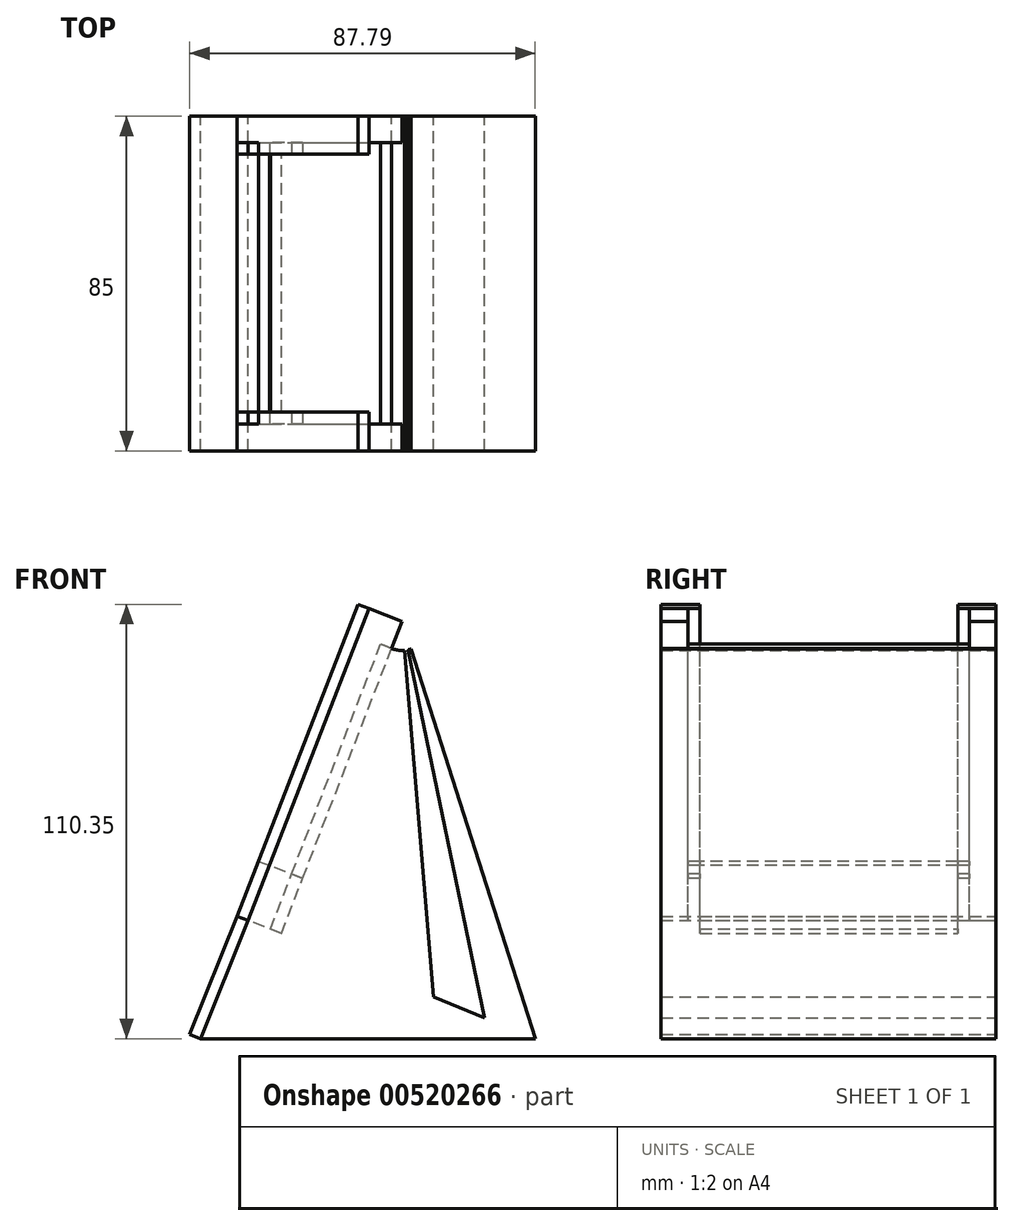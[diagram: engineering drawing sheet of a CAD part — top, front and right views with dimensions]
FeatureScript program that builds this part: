
annotation { "Feature Type Name" : "Feature", "Feature Type Description" : "" }
export const myFeature = defineFeature(function(context is Context, id is Id, definition is map)
    precondition{}
    {
        {
            var Q0;
            Q0=qCreatedBy(makeId("Front.planeOp"),FACE);
            var sketch = newSketch(context, id + "F0", { "sketchPlane" : qUnion([Q0])});
            skLineSegment(sketch, "E0", {"start": v(-20.42, 0) * mm, "end": v(-8.32, 30) * mm});
            skLineSegment(sketch, "E1", {"start": v(-8.32, 30) * mm, "end": v(64.58, 0) * mm});
            skLineSegment(sketch, "E2", {"start": v(64.58, 0) * mm, "end": v(-20.42, 0) * mm});
            skLineSegment(sketch, "E3", {"start": v(-8.32, 30) * mm, "end": v(22.36, 109.27) * mm});
            skLineSegment(sketch, "E4", {"start": v(22.36, 109.27) * mm, "end": v(30.76, 106.02) * mm});
            skLineSegment(sketch, "E5", {"start": v(30.76, 106.02) * mm, "end": v(64.58, 0) * mm});
            skLineSegment(sketch, "E6", {"start": v(-8.32, 30) * mm, "end": v(0, 26.58) * mm});
            skLineSegment(sketch, "E7", {"start": v(0, 26.58) * mm, "end": v(-8.32, 30) * mm});
            skLineSegment(sketch, "E8", {"start": v(0, 26.58) * mm, "end": v(30.76, 106.02) * mm});
            skLineSegment(sketch, "E9", {"start": v(12.92, 21.26) * mm, "end": v(30.76, 106.02) * mm});
            skLineSegment(sketch, "E10", {"start": v(25.83, 15.95) * mm, "end": v(30.76, 106.02) * mm});
            skLineSegment(sketch, "E11", {"start": v(30.76, 106.02) * mm, "end": v(38.75, 10.63) * mm});
            skLineSegment(sketch, "E12", {"start": v(51.67, 5.32) * mm, "end": v(30.76, 106.02) * mm});
            skArc(sketch, "E13", {"start": v(33, 98.99) * mm, "mid": v(30.53, 98.64) * mm, "end": v(28.1, 99.13) * mm});
            skSolve(sketch);
        }
        {
            var Q0;
            Q0=makeQuery(id+"F0.imprint","IMPRINT",FACE,{"disambiguationData":[TD([[makeQuery(id+"F0.imprint","IMPRINT",EDGE,{"derivedFrom":sQuery(id+"F0.wireOp",EDGE,"E3")}),-1.0]])]});
            var Q1;
            {var subQ1=sQuery(id+"F0.wireOp",EDGE,"E1");var subQ3=sQuery(id+"F0.wireOp",EDGE,"E9");var subQ4=makeQuery(id+"F0.imprint","INTERSECT",VERTEX,{"derivedFrom":[subQ1,subQ3]});Q1=makeQuery(id+"F0.imprint","IMPRINT",FACE,{"disambiguationData":[TD([[makeQuery(id+"F0.imprint","IMPRINT",EDGE,{"disambiguationData":[TD([[subQ4,-1.0]])],"derivedFrom":subQ3}),1.0]])]});}
            var Q2;
            {var subQ1=sQuery(id+"F0.wireOp",EDGE,"E9");var subQ3=sQuery(id+"F0.wireOp",EDGE,"E13");var subQ4=makeQuery(id+"F0.imprint","INTERSECT",VERTEX,{"derivedFrom":[subQ1,subQ3]});Q2=makeQuery(id+"F0.imprint","IMPRINT",FACE,{"disambiguationData":[TD([[makeQuery(id+"F0.imprint","IMPRINT",EDGE,{"disambiguationData":[TD([[subQ4,1.0]])],"derivedFrom":subQ3}),-1.0]])]});}
            var Q3;
            {var subQ1=sQuery(id+"F0.wireOp",EDGE,"E10");var subQ3=sQuery(id+"F0.wireOp",EDGE,"E13");var subQ4=makeQuery(id+"F0.imprint","INTERSECT",VERTEX,{"derivedFrom":[subQ1,subQ3]});Q3=makeQuery(id+"F0.imprint","IMPRINT",FACE,{"disambiguationData":[TD([[makeQuery(id+"F0.imprint","IMPRINT",EDGE,{"disambiguationData":[TD([[subQ4,1.0]])],"derivedFrom":subQ3}),-1.0]])]});}
            var Q4;
            {var subQ1=sQuery(id+"F0.wireOp",EDGE,"E8");var subQ3=sQuery(id+"F0.wireOp",EDGE,"E13");var subQ4=makeQuery(id+"F0.imprint","INTERSECT",VERTEX,{"derivedFrom":[subQ1,subQ3]});Q4=makeQuery(id+"F0.imprint","IMPRINT",FACE,{"disambiguationData":[TD([[makeQuery(id+"F0.imprint","IMPRINT",EDGE,{"disambiguationData":[TD([[subQ4,1.0]])],"derivedFrom":subQ3}),-1.0]])]});}
            var Q5;
            {var subQ1=sQuery(id+"F0.wireOp",EDGE,"E11");var subQ3=sQuery(id+"F0.wireOp",EDGE,"E13");var subQ4=makeQuery(id+"F0.imprint","INTERSECT",VERTEX,{"derivedFrom":[subQ1,subQ3]});Q5=makeQuery(id+"F0.imprint","IMPRINT",FACE,{"disambiguationData":[TD([[makeQuery(id+"F0.imprint","IMPRINT",EDGE,{"disambiguationData":[TD([[subQ4,1.0]])],"derivedFrom":subQ3}),-1.0]])]});}
            var Q6;
            {var subQ1=sQuery(id+"F0.wireOp",EDGE,"E5");var subQ3=sQuery(id+"F0.wireOp",EDGE,"E13");var subQ4=makeQuery(id+"F0.imprint","INTERSECT",VERTEX,{"derivedFrom":[subQ1,subQ3]});Q6=makeQuery(id+"F0.imprint","IMPRINT",FACE,{"disambiguationData":[TD([[makeQuery(id+"F0.imprint","IMPRINT",EDGE,{"disambiguationData":[TD([[subQ4,-1.0]])],"derivedFrom":subQ3}),-1.0]])]});}
            var Q7;
            {var subQ0=sQuery(id+"F0.wireOp",EDGE,"E10");var subQ1=sQuery(id+"F0.wireOp",EDGE,"E1");var subQ2=makeQuery(id+"F0.imprint","INTERSECT",VERTEX,{"derivedFrom":[subQ1,subQ0]});Q7=makeQuery(id+"F0.imprint","IMPRINT",FACE,{"disambiguationData":[TD([[makeQuery(id+"F0.imprint","IMPRINT",EDGE,{"disambiguationData":[TD([[subQ2,-1.0]])],"derivedFrom":subQ1}),1.0]])]});}
            var Q8;
            {var subQ1=sQuery(id+"F0.wireOp",EDGE,"E1");var subQ3=sQuery(id+"F0.wireOp",EDGE,"E12");var subQ4=makeQuery(id+"F0.imprint","INTERSECT",VERTEX,{"derivedFrom":[subQ1,subQ3]});Q8=makeQuery(id+"F0.imprint","IMPRINT",FACE,{"disambiguationData":[TD([[makeQuery(id+"F0.imprint","IMPRINT",EDGE,{"disambiguationData":[TD([[subQ4,-1.0]])],"derivedFrom":subQ3}),-1.0]])]});}
            var Q9;
            Q9=makeQuery(id+"F0.imprint","IMPRINT",FACE,{"disambiguationData":[TD([[makeQuery(id+"F0.imprint","IMPRINT",EDGE,{"derivedFrom":sQuery(id+"F0.wireOp",EDGE,"E0")}),-1.0]])]});
            extrude(context, id + "F1", {"entities" : qUnion([Q0, Q1, Q2, Q3, Q4, Q5, Q6, Q7, Q8, Q9]), "endBound" : BoundingType.SYMMETRIC, "depth" : 85 * mm, "offsetDistance" : 25 * mm});
        }
        {
            var Q0;
            Q0=makeQuery(id+"F1.opExtrude","SWEPT_FACE",FACE,{"disambiguationData":[OSD([sQuery(id+"F0.wireOp",EDGE,"E3")])]});
            var sketch = newSketch(context, id + "F2", { "sketchPlane" : qUnion([Q0])});
            skLineSegment(sketch, "E14.bottom", {"start": v(-35.85, 24.97) * mm, "end": v(35.65, 24.97) * mm});
            skLineSegment(sketch, "E14.top", {"start": v(-35.85, 121.84) * mm, "end": v(35.65, 121.84) * mm});
            skLineSegment(sketch, "E14.left", {"start": v(-35.85, 24.97) * mm, "end": v(-35.85, 121.84) * mm});
            skLineSegment(sketch, "E14.right", {"start": v(35.65, 24.97) * mm, "end": v(35.65, 121.84) * mm});
            skLineSegment(sketch, "E15.bottom", {"start": v(-0.1, 24.97) * mm, "end": v(35.65, 24.97) * mm});
            skLineSegment(sketch, "E15.right", {"start": v(35.65, 24.97) * mm, "end": v(35.65, 35.08) * mm});
            skLineSegment(sketch, "E16.bottom", {"start": v(-35.85, 24.97) * mm, "end": v(-0.1, 24.97) * mm});
            skLineSegment(sketch, "E16.left", {"start": v(-35.85, 24.97) * mm, "end": v(-35.85, 35.08) * mm});
            skLineSegment(sketch, "E17.top", {"start": v(-35.85, 39.97) * mm, "end": v(35.65, 39.97) * mm});
            skLineSegment(sketch, "E17.left", {"start": v(-35.85, 24.97) * mm, "end": v(-35.85, 39.97) * mm});
            skLineSegment(sketch, "E17.right", {"start": v(35.65, 24.97) * mm, "end": v(35.65, 39.97) * mm});
            skLineSegment(sketch, "E18.bottom", {"start": v(-35.85, 24.97) * mm, "end": v(-32.85, 24.97) * mm});
            skLineSegment(sketch, "E18.top", {"start": v(-35.85, 109.97) * mm, "end": v(-32.85, 109.97) * mm});
            skLineSegment(sketch, "E18.left", {"start": v(-35.85, 24.97) * mm, "end": v(-35.85, 109.97) * mm});
            skLineSegment(sketch, "E18.right", {"start": v(-32.85, 24.97) * mm, "end": v(-32.85, 109.97) * mm});
            skLineSegment(sketch, "E19.bottom", {"start": v(35.65, 24.97) * mm, "end": v(32.65, 24.97) * mm});
            skLineSegment(sketch, "E19.top", {"start": v(35.65, 109.97) * mm, "end": v(32.65, 109.97) * mm});
            skLineSegment(sketch, "E19.left", {"start": v(35.65, 24.97) * mm, "end": v(35.65, 109.97) * mm});
            skLineSegment(sketch, "E19.right", {"start": v(32.65, 24.97) * mm, "end": v(32.65, 109.97) * mm});
            skSolve(sketch);
        }
        {
            var Q0;
            {var subQ5=sQuery(id+"F2.wireOp",EDGE,"E19.top");Q0=makeQuery(id+"F2.imprint","IMPRINT",FACE,{"disambiguationData":[TD([[makeQuery(id+"F2.imprint","IMPRINT",EDGE,{"derivedFrom":subQ5}),1.0]])]});}
            var Q1;
            {var subQ0=sQuery(id+"F2.wireOp",EDGE,"E18.right");var subQ1=sQuery(id+"F2.wireOp",EDGE,"E17.top");var subQ2=makeQuery(id+"F2.imprint","INTERSECT",VERTEX,{"derivedFrom":[subQ1,subQ0]});Q1=makeQuery(id+"F2.imprint","IMPRINT",FACE,{"disambiguationData":[TD([[makeQuery(id+"F2.imprint","IMPRINT",EDGE,{"disambiguationData":[TD([[subQ2,-1.0]])],"derivedFrom":subQ1}),1.0]])]});}
            var Q2;
            {var subQ5=sQuery(id+"F2.wireOp",EDGE,"E18.top");Q2=makeQuery(id+"F2.imprint","IMPRINT",FACE,{"disambiguationData":[TD([[makeQuery(id+"F2.imprint","IMPRINT",EDGE,{"derivedFrom":subQ5}),1.0]])]});}
            var Q3;
            {var subQ0=sQuery(id+"F2.wireOp",EDGE,"E14.bottom");Q3=makeQuery(id+"F2.imprint","IMPRINT",FACE,{"disambiguationData":[TD([[makeQuery(id+"F2.imprint","IMPRINT",EDGE,{"derivedFrom":subQ0}),-1.0]])]});}
            var Q4;
            {var subQ4=sQuery(id+"F2.wireOp",EDGE,"E18.bottom");Q4=makeQuery(id+"F2.imprint","IMPRINT",FACE,{"disambiguationData":[TD([[makeQuery(id+"F2.imprint","IMPRINT",EDGE,{"derivedFrom":subQ4}),-1.0]])]});}
            var Q5;
            {var subQ6=sQuery(id+"F2.wireOp",EDGE,"E19.bottom");Q5=makeQuery(id+"F2.imprint","IMPRINT",FACE,{"disambiguationData":[TD([[makeQuery(id+"F2.imprint","IMPRINT",EDGE,{"derivedFrom":subQ6}),-1.0]])]});}
            extrude(context, id + "F3", {"entities" : qUnion([Q0, Q1, Q2, Q3, Q4, Q5]), "operationType" : NewBodyOperationType.REMOVE, "oppositeDirection" : true, "depth" : 9 * mm, "offsetDistance" : 25 * mm});
        }
        {
            var Q0;
            Q0=makeQuery(id+"F3.boolean.opBoolean","COPY",FACE,{"derivedFrom":makeQuery(id+"F3.opExtrude","CAP_FACE",FACE,{"disambiguationData":[OSD([sQuery(id+"F0.wireOp",EDGE,"E3"),sQuery(id+"F0.wireOp",EDGE,"E4"),sQuery(id+"F2.wireOp",EDGE,"E14.bottom"),sQuery(id+"F2.wireOp",EDGE,"E18.bottom"),sQuery(id+"F2.wireOp",EDGE,"E18.top"),sQuery(id+"F2.wireOp",EDGE,"E18.left"),sQuery(id+"F2.wireOp",EDGE,"E19.bottom"),sQuery(id+"F2.wireOp",EDGE,"E19.top"),sQuery(id+"F2.wireOp",EDGE,"E19.left")])],"isStart":false})});
            var Q1;
            {var subQ5=sQuery(id+"F2.wireOp",EDGE,"E18.top");Q1=makeQuery(id+"F2.imprint","IMPRINT",FACE,{"disambiguationData":[TD([[makeQuery(id+"F2.imprint","IMPRINT",EDGE,{"derivedFrom":subQ5}),1.0]])]});}
            var Q2;
            {var subQ4=sQuery(id+"F2.wireOp",EDGE,"E18.bottom");Q2=makeQuery(id+"F2.imprint","IMPRINT",FACE,{"disambiguationData":[TD([[makeQuery(id+"F2.imprint","IMPRINT",EDGE,{"derivedFrom":subQ4}),-1.0]])]});}
            var Q3;
            {var subQ0=sQuery(id+"F2.wireOp",EDGE,"E14.bottom");Q3=makeQuery(id+"F2.imprint","IMPRINT",FACE,{"disambiguationData":[TD([[makeQuery(id+"F2.imprint","IMPRINT",EDGE,{"derivedFrom":subQ0}),-1.0]])]});}
            var Q4;
            {var subQ6=sQuery(id+"F2.wireOp",EDGE,"E19.bottom");Q4=makeQuery(id+"F2.imprint","IMPRINT",FACE,{"disambiguationData":[TD([[makeQuery(id+"F2.imprint","IMPRINT",EDGE,{"derivedFrom":subQ6}),-1.0]])]});}
            var Q5;
            {var subQ5=sQuery(id+"F2.wireOp",EDGE,"E19.top");Q5=makeQuery(id+"F2.imprint","IMPRINT",FACE,{"disambiguationData":[TD([[makeQuery(id+"F2.imprint","IMPRINT",EDGE,{"derivedFrom":subQ5}),1.0]])]});}
            var Q6;
            {var subQ0=sQuery(id+"F0.wireOp",EDGE,"E3");var subQ1=makeQuery(id+"F1.opExtrude","CAP_EDGE",EDGE,{"disambiguationData":[OSD([subQ0])],"isStart":true});Q6=makeQuery(id+"F2.imprint","IMPRINT",FACE,{"disambiguationData":[TD([[makeQuery(id+"F2.imprint","IMPRINT",EDGE,{"derivedFrom":subQ1}),-1.0]])]});}
            var Q7;
            {var subQ1=sQuery(id+"F0.wireOp",EDGE,"E3");var subQ5=makeQuery(id+"F1.opExtrude","CAP_EDGE",EDGE,{"disambiguationData":[OSD([subQ1])],"isStart":false});Q7=makeQuery(id+"F2.imprint","IMPRINT",FACE,{"disambiguationData":[TD([[makeQuery(id+"F2.imprint","IMPRINT",EDGE,{"derivedFrom":subQ5}),1.0]])]});}
            var Q8;
            Q8=makeQuery(id+"F1.opExtrude","SWEPT_FACE",FACE,{"disambiguationData":[OSD([sQuery(id+"F0.wireOp",EDGE,"E0")])]});
            extrude(context, id + "F4", {"entities" : qUnion([Q0, Q1, Q2, Q3, Q4, Q5, Q6, Q7, Q8]), "operationType" : NewBodyOperationType.ADD, "depth" : 3 * mm, "offsetDistance" : 25 * mm});
        }
    });
